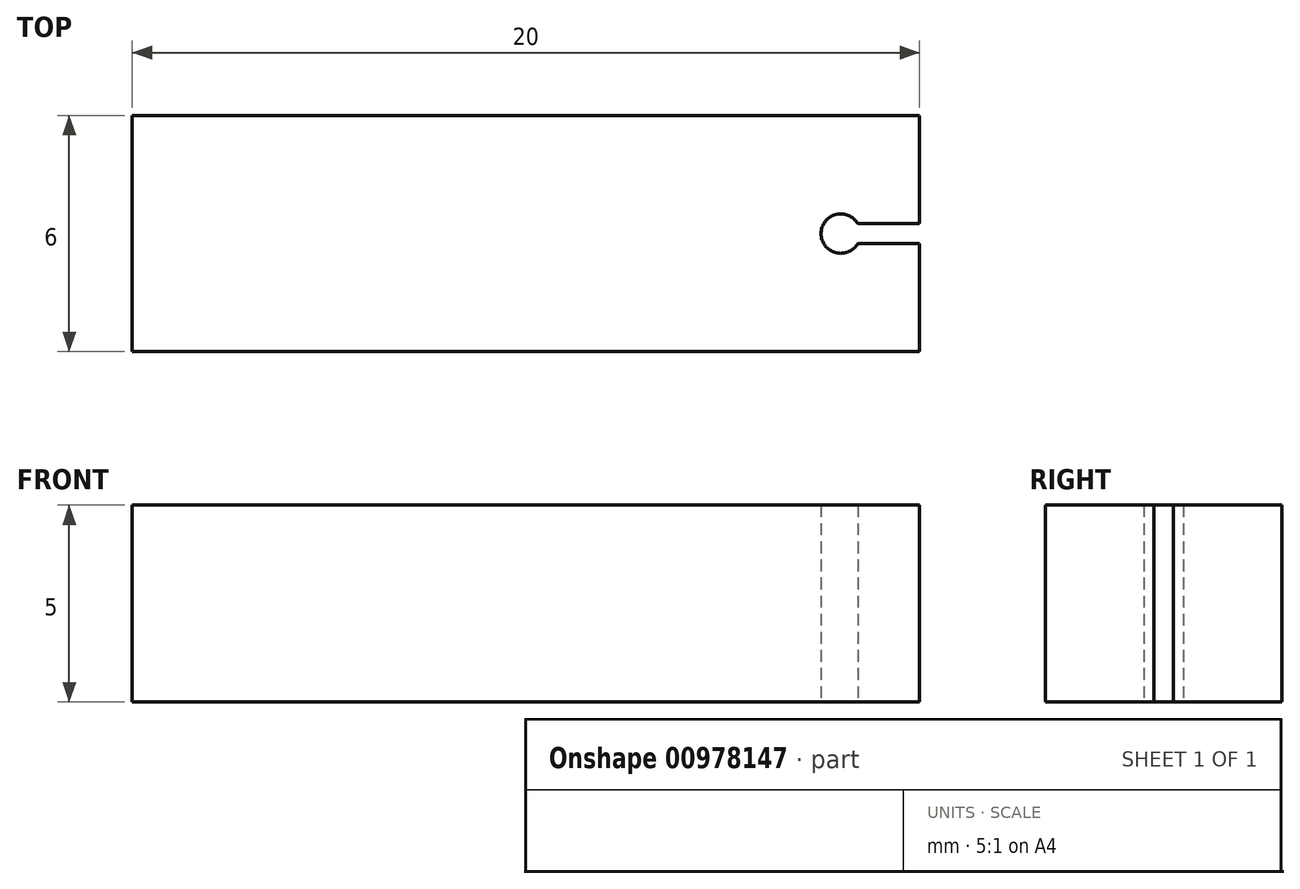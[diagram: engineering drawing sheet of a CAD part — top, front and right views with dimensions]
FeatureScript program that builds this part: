
annotation { "Feature Type Name" : "Feature", "Feature Type Description" : "" }
export const myFeature = defineFeature(function(context is Context, id is Id, definition is map)
    precondition{}
    {
        {
            var Q0;
            Q0=qCreatedBy(makeId("Top.planeOp"),FACE);
            var sketch = newSketch(context, id + "F0", { "sketchPlane" : qUnion([Q0])});
            skLineSegment(sketch, "E0.bottom", {"start": v(10, -3) * mm, "end": v(-10, -3) * mm});
            skLineSegment(sketch, "E0.top", {"start": v(10, 3) * mm, "end": v(-10, 3) * mm});
            skLineSegment(sketch, "E0.left", {"start": v(10, -3) * mm, "end": v(10, -0.25) * mm});
            skLineSegment(sketch, "E0.right", {"start": v(-10, -3) * mm, "end": v(-10, 3) * mm});
            skPoint(sketch, "E0.middle", {"position": v(0, 0) * mm});
            skArc(sketch, "E1", {"start": v(8.43, 0.25) * mm, "mid": v(7.5, 0) * mm, "end": v(8.43, -0.25) * mm});
            skLineSegment(sketch, "E2.bottom", {"start": v(8.43, -0.25) * mm, "end": v(10, -0.25) * mm});
            skLineSegment(sketch, "E2.top", {"start": v(8.43, 0.25) * mm, "end": v(10, 0.25) * mm});
            skPoint(sketch, "E2.middle", {"position": v(10, 0) * mm});
            skPoint(sketch, "E3.orphan", {"position": v(8.23, 0.25) * mm});
            skPoint(sketch, "E4.orphan", {"position": v(8.23, -0.25) * mm});
            skLineSegment(sketch, "E5.trimOffspring", {"start": v(10, 0.25) * mm, "end": v(10, 3) * mm});
            skSolve(sketch);
        }
        {
            var Q0;
            Q0 = qSketchRegion(id + "F0", true);
            extrude(context, id + "F1", {"entities" : qUnion([Q0]), "depth" : 5 * mm, "offsetDistance" : 25 * mm});
        }
    });
